# Revit family: KompaktSystem
name_source: partatom
category: Drzwi
revit_build: Autodesk Revit 2016 (Build: 20150714_1515(x64)
units: mm (PartAtom-declared; Revit-internal decimal feet)

## family parameters
Obiekt nadrzędny = Ściana
Punkt obliczania pomieszczeń = Nie
Tnij formami wycięć po wczytaniu = Nie
Współdzielony = Nie
Zawsze pionowo = Tak

## types (5) — shared parameters
Funkcja = Wewnętrzna
Hs = 2030 mm  [stored 6.6601 ft]
Informacja = Własność Porta KMI Poland, wszelkie prawa zastrzeżone.
Konstrukcja analityczna = <Brak>
Producent = PORTA KMI POLAND
URL = www.porta.com.pl
Wysokość = 2075 mm
Zakończenie ściany = Wg obiektu nadrzędnego

## per-type parameters (varying)
| type | 1 | Ss | Szerokość |
| 60 | -753 mm | 644 mm  [stored 2.11286 ft] | 670 mm |
| 70 | -853 mm | 744 mm | 770 mm |
| 80 | -953 mm | 844 mm | 870 mm |
| 90 | -1053 mm  [stored -3.45472 ft] | 944 mm | 970 mm  [stored 3.18241 ft] |
| 100 | -1153 mm | 1044 mm | 1070 mm |

note: [stored X ft] marks values corroborated as IEEE doubles in the binary element streams (Revit-internal decimal feet)

## geometry (parser evidence)
native form markers: Blend x2
no freeform markers — native parametric forms only
